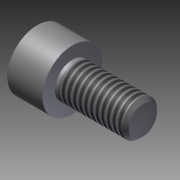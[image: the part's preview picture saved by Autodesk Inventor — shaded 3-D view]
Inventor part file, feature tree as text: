
AUTODESK INVENTOR PART (.ipt)
format: ipt  version: 2011 SP1 (Build 150282100, 282)  size: 115,200 bytes
history: native  units: mm
features: other x14, sketch x3, revolve x2, thread x1, extrude x1
ambient origin geometry x8: Origin, YZ Plane, XZ Plane, XY Plane, X Axis, Y Axis, Z Axis, Center Point
bodies: Solid1 (feature_tree)
feature tree (21):
  revolve  "Revolution1"  [1 undecoded]
  thread  "Thread1"  [1 undecoded]
  revolve  "Revolution2"  [1 undecoded]
  extrude  "Extrusion1"  [1 undecoded]
  other  "bolt_XY"
  other  "bolt_YZ"
  other  "bolt_ZX"
  other  "bolt_X"
  other  "bolt_Y"
  other  "bolt_Z"
  other  "bolt_Center"
  other  "nut_XY"
  other  "nut_YZ"
  other  "nut_ZX"
  other  "nut_X"
  other  "nut_Y"
  other  "nut_Z"
  other  "nut_Center"
  sketch  "Sketch_1"  dims[d0=360.0deg d1=9.5mm d2=0.5mm d3=360.0deg]
  sketch  "Sketch_4"
  sketch  "Sketch_3"  dims[d4=2.5mm d5=0.0mm]
note: 4 required parameter values undecoded (feature->parameter linkage not recoverable at this tier; creation-order binding heuristic only, values carry confidence <= 0.55)